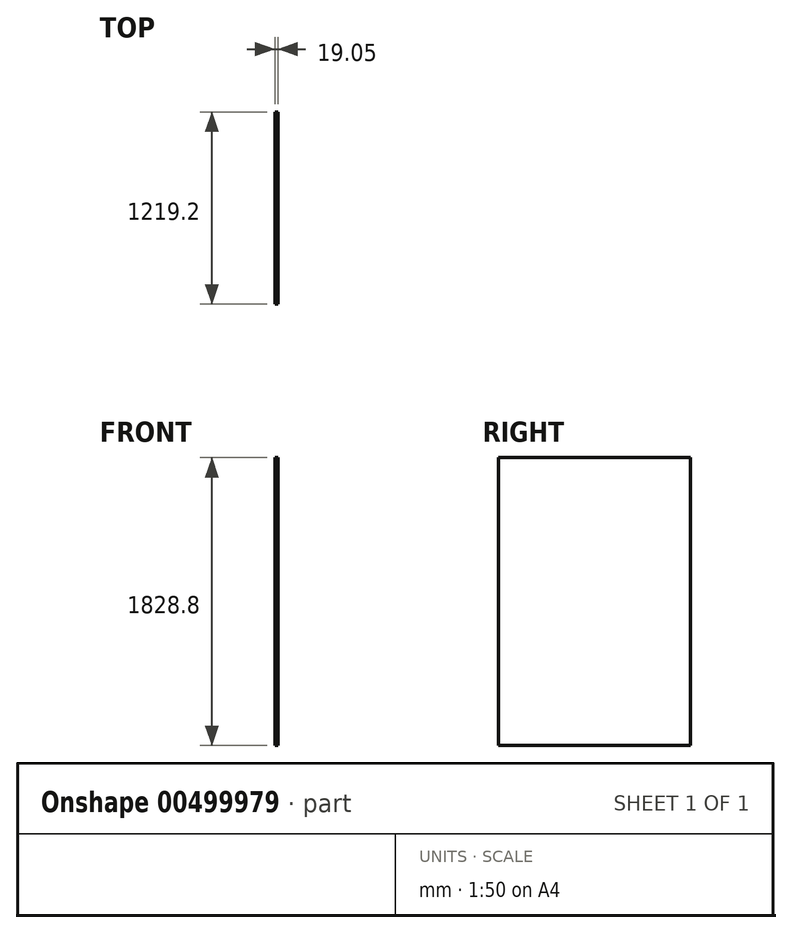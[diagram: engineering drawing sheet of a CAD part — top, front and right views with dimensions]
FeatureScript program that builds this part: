
annotation { "Feature Type Name" : "Feature", "Feature Type Description" : "" }
export const myFeature = defineFeature(function(context is Context, id is Id, definition is map)
    precondition{}
    {
        {
            var Q0;
            Q0=qCreatedBy(makeId("Right.planeOp"),FACE);
            var sketch = newSketch(context, id + "F0", { "sketchPlane" : qUnion([Q0])});
            skLineSegment(sketch, "E0.bottom", {"start": v(-609.6, 609.6) * mm, "end": v(609.6, 609.6) * mm});
            skLineSegment(sketch, "E0.top", {"start": v(-609.6, -609.6) * mm, "end": v(609.6, -609.6) * mm});
            skLineSegment(sketch, "E0.left", {"start": v(-609.6, 609.6) * mm, "end": v(-609.6, -609.6) * mm});
            skLineSegment(sketch, "E0.right", {"start": v(609.6, 609.6) * mm, "end": v(609.6, -609.6) * mm});
            skPoint(sketch, "E0.middle", {"position": v(0, 0) * mm});
            skLineSegment(sketch, "E1.top", {"start": v(-609.6, -1219.2) * mm, "end": v(609.6, -1219.2) * mm});
            skLineSegment(sketch, "E1.left", {"start": v(-609.6, -609.6) * mm, "end": v(-609.6, -1219.2) * mm});
            skLineSegment(sketch, "E1.right", {"start": v(609.6, -609.6) * mm, "end": v(609.6, -1219.2) * mm});
            skSolve(sketch);
        }
        {
            var Q0;
            Q0 = qSketchRegion(id + "F0", true);
            extrude(context, id + "F1", {"entities" : qUnion([Q0]), "depth" : 19.05 * mm, "offsetDistance" : 25.4 * mm});
        }
    });
